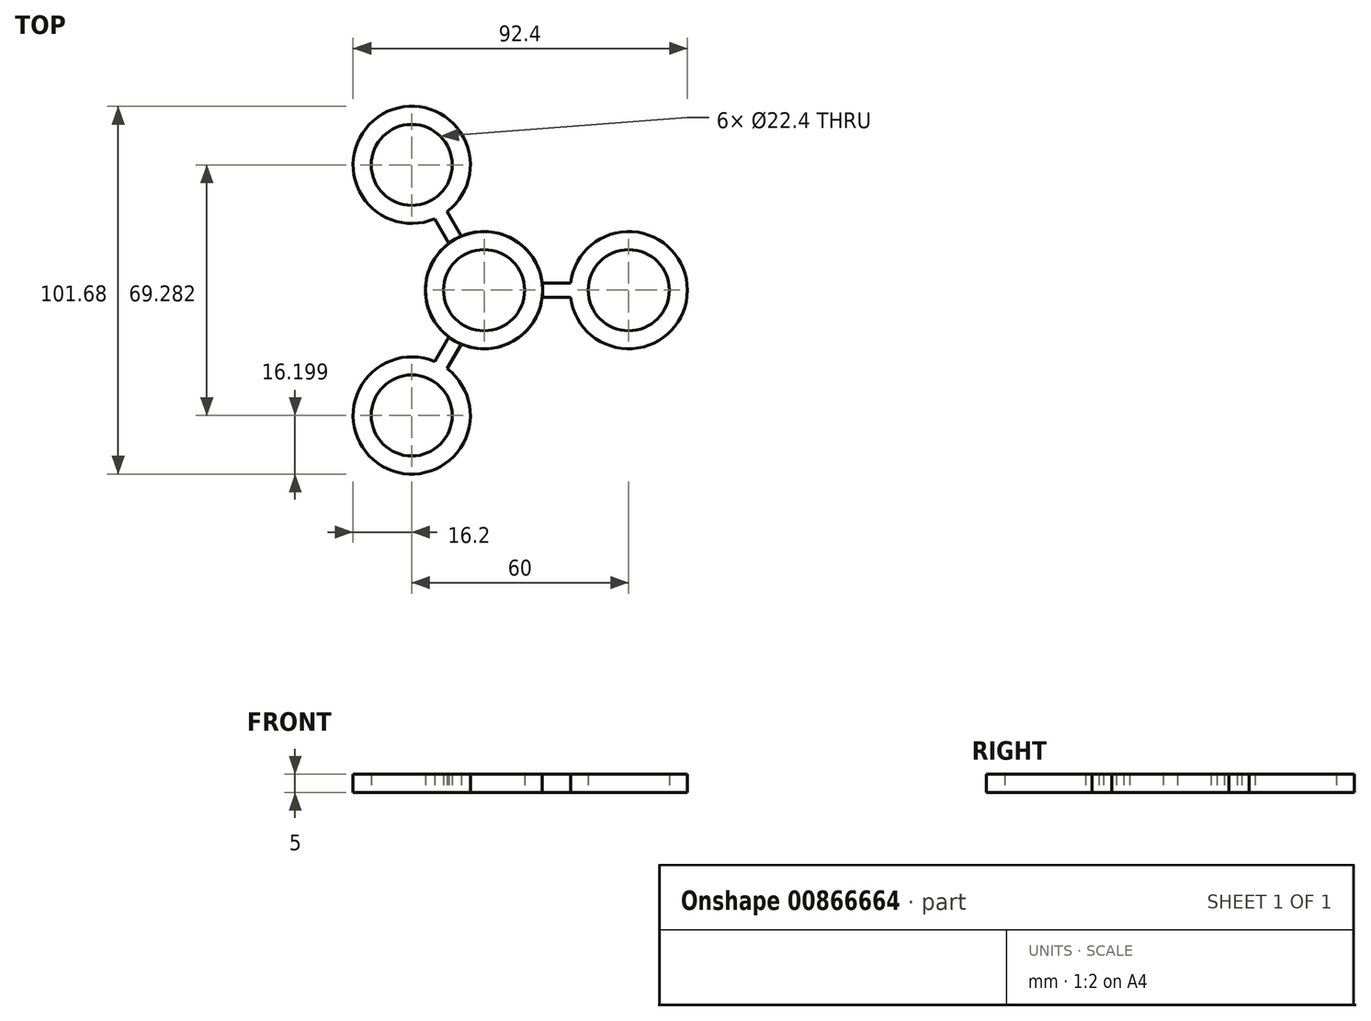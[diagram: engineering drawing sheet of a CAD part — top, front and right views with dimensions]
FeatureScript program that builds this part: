
annotation { "Feature Type Name" : "Feature", "Feature Type Description" : "" }
export const myFeature = defineFeature(function(context is Context, id is Id, definition is map)
    precondition{}
    {
        {
            var Q0;
            Q0=qCreatedBy(makeId("Top.planeOp"),FACE);
            var sketch = newSketch(context, id + "F0", { "sketchPlane" : qUnion([Q0])});
            skCircle(sketch, "E0", {"center": v(0, 0) * mm, "radius": 11.2 * mm});
            skCircle(sketch, "E1.0", {"center": v(0, 0) * mm, "radius": 16.2 * mm});
            skSolve(sketch);
        }
        {
            var Q0;
            Q0=makeQuery(id+"F0.imprint","IMPRINT",FACE,{"disambiguationData":[TD([[makeQuery(id+"F0.imprint","IMPRINT",EDGE,{"derivedFrom":sQuery(id+"F0.wireOp",EDGE,"E0")}),-1.0]])]});
            extrude(context, id + "F1", {"entities" : qUnion([Q0]), "depth" : 5 * mm, "offsetDistance" : 25 * mm});
        }
        {
            var Q0;
            Q0=qCreatedBy(makeId("Top.planeOp"),FACE);
            var sketch = newSketch(context, id + "F2", { "sketchPlane" : qUnion([Q0])});
            skLineSegment(sketch, "E2.bottom", {"start": v(12.5, -2) * mm, "end": v(23.92, -2) * mm});
            skLineSegment(sketch, "E2.top", {"start": v(12.5, 2) * mm, "end": v(23.92, 2) * mm});
            skPoint(sketch, "E2.middle", {"position": v(20, 0) * mm});
            skLineSegment(sketch, "E3", {"start": v(12.5, -2) * mm, "end": v(12.5, 2) * mm});
            skPoint(sketch, "E4.orphan", {"position": v(0, 0) * mm});
            skPoint(sketch, "E5.orphan", {"position": v(40, 0) * mm});
            skPoint(sketch, "E6.orphan", {"position": v(0, 2) * mm});
            skPoint(sketch, "E2.left.start.orphan", {"position": v(0, -2) * mm});
            skCircle(sketch, "E7", {"center": v(40, 0) * mm, "radius": 11.2 * mm});
            skArc(sketch, "E8.0", {"start": v(23.92, -2) * mm, "mid": v(56.2, 0) * mm, "end": v(23.92, 2) * mm});
            skPoint(sketch, "E9.orphan", {"position": v(40, 2) * mm});
            skPoint(sketch, "E2.right.start.orphan", {"position": v(40, -2) * mm});
            skSolve(sketch);
        }
        {
            var Q0;
            Q0 = qSketchRegion(id + "F2", true);
            extrude(context, id + "F3", {"entities" : qUnion([Q0]), "operationType" : NewBodyOperationType.ADD, "depth" : 5 * mm, "offsetDistance" : 25 * mm});
        }
        {
            var Q0;
            Q0=makeQuery(id+"F1.opExtrude","SWEPT_BODY",BODY,{"disambiguationData":[OSD([sQuery(id+"F0.wireOp",EDGE,"E0"),sQuery(id+"F0.wireOp",EDGE,"E1.0")])]});
            var Q1;
            Q1=makeQuery(id+"F1.opExtrude","CAP_EDGE",EDGE,{"disambiguationData":[OSD([sQuery(id+"F0.wireOp",EDGE,"E0")])],"isStart":false});
            circularPattern(context, id + "F4", {"entities" : qUnion([Q0]), "axis" : qUnion([Q1]), "angle" : 360 * degree, "instanceCount" : 3, "oppositeDirection" : true, "equalSpace" : true});
        }
    });
